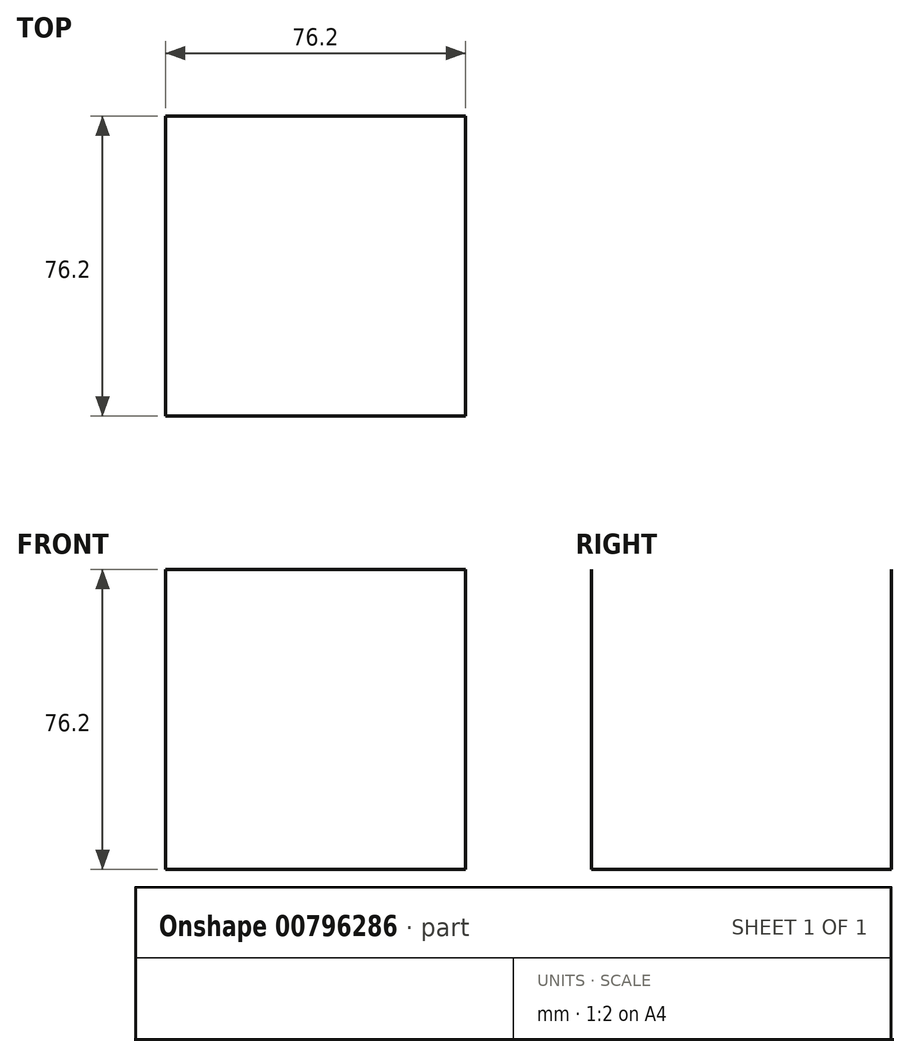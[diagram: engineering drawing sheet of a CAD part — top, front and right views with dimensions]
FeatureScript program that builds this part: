
annotation { "Feature Type Name" : "Feature", "Feature Type Description" : "" }
export const myFeature = defineFeature(function(context is Context, id is Id, definition is map)
    precondition{}
    {
        {
            var Q0;
            Q0=qCreatedBy(makeId("Top.planeOp"),FACE);
            var sketch = newSketch(context, id + "F0", { "sketchPlane" : qUnion([Q0])});
            skLineSegment(sketch, "E0.bottom", {"start": v(-38.1, 38.1) * mm, "end": v(38.1, 38.1) * mm});
            skLineSegment(sketch, "E0.top", {"start": v(-38.1, -38.1) * mm, "end": v(38.1, -38.1) * mm});
            skLineSegment(sketch, "E0.left", {"start": v(-38.1, 38.1) * mm, "end": v(-38.1, -38.1) * mm});
            skLineSegment(sketch, "E0.right", {"start": v(38.1, 38.1) * mm, "end": v(38.1, -38.1) * mm});
            skPoint(sketch, "E0.middle", {"position": v(0, 0) * mm});
            skSolve(sketch);
        }
        {
            var Q0;
            Q0=makeQuery(id+"F0.imprint","IMPRINT",FACE,{"disambiguationData":[TD([[makeQuery(id+"F0.imprint","IMPRINT",EDGE,{"derivedFrom":sQuery(id+"F0.wireOp",EDGE,"E0.bottom")}),-1.0]])]});
            extrude(context, id + "F1", {"entities" : qUnion([Q0]), "depth" : 1 / 203.2 * mm, "offsetDistance" : 25.4 * mm});
        }
        {
            var Q0;
            Q0=makeQuery(id+"F1.opExtrude","SWEPT_FACE",FACE,{"disambiguationData":[OSD([sQuery(id+"F0.wireOp",EDGE,"E0.top")])]});
            var sketch = newSketch(context, id + "F2", { "sketchPlane" : qUnion([Q0])});
            skLineSegment(sketch, "E1.top", {"start": v(-38.1, 76.2) * mm, "end": v(38.1, 76.2) * mm});
            skLineSegment(sketch, "E2.bottom", {"start": v(38.1, 0) * mm, "end": v(-38.1, 0) * mm});
            skLineSegment(sketch, "E2.top", {"start": v(38.1, 76.2) * mm, "end": v(-38.1, 76.2) * mm});
            skLineSegment(sketch, "E2.left", {"start": v(38.1, 0) * mm, "end": v(38.1, 76.2) * mm});
            skLineSegment(sketch, "E2.right", {"start": v(-38.1, 0) * mm, "end": v(-38.1, 76.2) * mm});
            skSolve(sketch);
        }
        {
            var Q0;
            {var subQ0=sQuery(id+"F2.wireOp",EDGE,"E1.top");Q0=makeQuery(id+"F2.imprint","IMPRINT",FACE,{"disambiguationData":[TD([[makeQuery(id+"F2.imprint","IMPRINT",EDGE,{"derivedFrom":subQ0}),-1.0]])]});}
            extrude(context, id + "F3", {"entities" : qUnion([Q0]), "operationType" : NewBodyOperationType.ADD, "depth" : 1 / 203.2 * mm, "offsetDistance" : 25.4 * mm});
        }
        {
            var Q0;
            Q0 = qSketchRegion(id + "F2", true);
            extrude(context, id + "F4", {"entities" : qUnion([Q0]), "operationType" : NewBodyOperationType.ADD, "depth" : 1 / 203.2 * mm, "offsetDistance" : 25.4 * mm});
        }
        {
            var Q0;
            Q0=makeQuery(id+"F1.opExtrude","SWEPT_FACE",FACE,{"disambiguationData":[OSD([sQuery(id+"F0.wireOp",EDGE,"E0.bottom")])]});
            var sketch = newSketch(context, id + "F5", { "sketchPlane" : qUnion([Q0])});
            skLineSegment(sketch, "E3.bottom", {"start": v(-38.1, 0) * mm, "end": v(38.1, 0) * mm});
            skLineSegment(sketch, "E3.top", {"start": v(-38.1, 76.2) * mm, "end": v(38.1, 76.2) * mm});
            skLineSegment(sketch, "E3.left", {"start": v(-38.1, 0) * mm, "end": v(-38.1, 76.2) * mm});
            skLineSegment(sketch, "E3.right", {"start": v(38.1, 0) * mm, "end": v(38.1, 76.2) * mm});
            skSolve(sketch);
        }
        {
            var Q0;
            Q0 = qSketchRegion(id + "F5", true);
            extrude(context, id + "F6", {"entities" : qUnion([Q0]), "operationType" : NewBodyOperationType.ADD, "depth" : 1 / 203.2 * mm, "offsetDistance" : 25.4 * mm});
        }
    });
